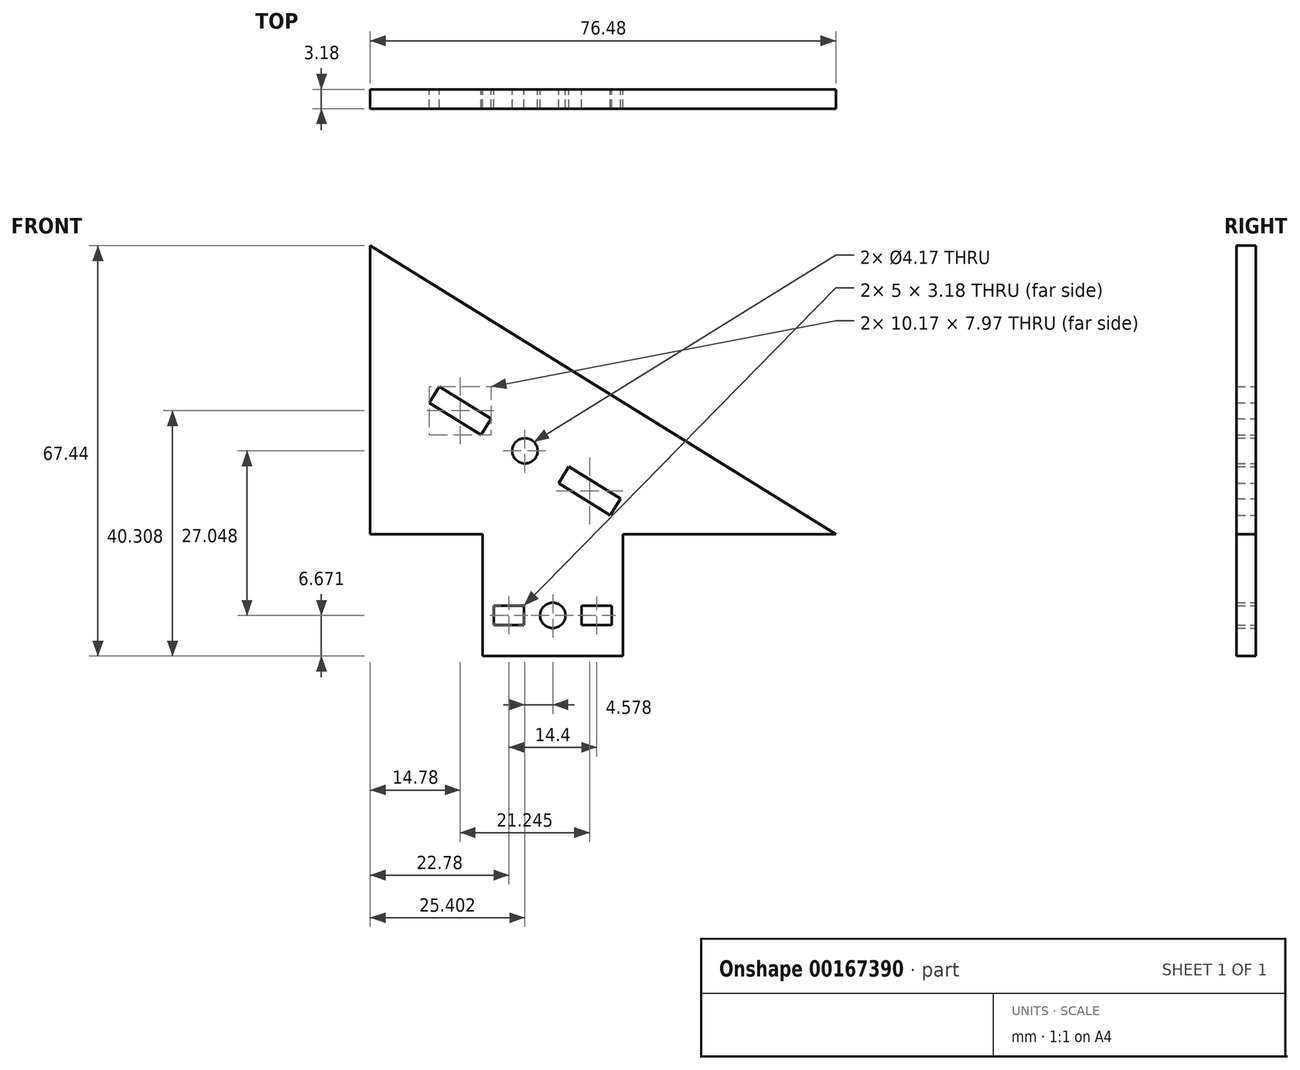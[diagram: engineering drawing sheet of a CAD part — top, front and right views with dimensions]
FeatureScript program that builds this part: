
annotation { "Feature Type Name" : "Feature", "Feature Type Description" : "" }
export const myFeature = defineFeature(function(context is Context, id is Id, definition is map)
    precondition{}
    {
        {
            var Q0;
            Q0=qCreatedBy(makeId("Front.planeOp"),FACE);
            var sketch = newSketch(context, id + "F0", { "sketchPlane" : qUnion([Q0])});
            skLineSegment(sketch, "E0", {"start": v(0, -17.4) * mm, "end": v(-11.5, -17.4) * mm});
            skLineSegment(sketch, "E1.MirrorCS", {"start": v(0, -17.4) * mm, "end": v(11.5, -17.4) * mm});
            skLineSegment(sketch, "E2", {"start": v(-11.5, -17.4) * mm, "end": v(-11.5, 2.6) * mm});
            skLineSegment(sketch, "E3", {"start": v(-9.7, -12.32) * mm, "end": v(-9.7, -9.14) * mm});
            skLineSegment(sketch, "E4", {"start": v(-9.7, -9.14) * mm, "end": v(-4.7, -9.14) * mm});
            skLineSegment(sketch, "E5", {"start": v(-9.7, -12.32) * mm, "end": v(-4.7, -12.32) * mm});
            skLineSegment(sketch, "E6", {"start": v(-4.7, -12.32) * mm, "end": v(-4.7, -9.14) * mm});
            skCircle(sketch, "E7", {"center": v(0, -10.73) * mm, "radius": 2.08 * mm});
            skLineSegment(sketch, "E8.MirrorCS", {"start": v(9.7, -12.32) * mm, "end": v(9.7, -9.14) * mm});
            skLineSegment(sketch, "E9.MirrorCS", {"start": v(9.7, -9.14) * mm, "end": v(4.7, -9.14) * mm});
            skLineSegment(sketch, "E10.MirrorCS", {"start": v(9.7, -12.32) * mm, "end": v(4.7, -12.32) * mm});
            skLineSegment(sketch, "E11.MirrorCS", {"start": v(4.7, -12.32) * mm, "end": v(4.7, -9.14) * mm});
            skLineSegment(sketch, "E12.MirrorCS", {"start": v(11.5, -17.4) * mm, "end": v(11.5, 2.6) * mm});
            skLineSegment(sketch, "E13", {"start": v(11.5, 2.6) * mm, "end": v(46.5, 2.6) * mm});
            skLineSegment(sketch, "E14", {"start": v(46.5, 2.6) * mm, "end": v(-29.98, 50.04) * mm});
            skLineSegment(sketch, "E15", {"start": v(-29.98, 50.04) * mm, "end": v(-29.98, 2.6) * mm});
            skLineSegment(sketch, "E16", {"start": v(-29.98, 2.6) * mm, "end": v(-11.5, 2.6) * mm});
            skLineSegment(sketch, "E17", {"start": v(-18.61, 26.9) * mm, "end": v(-10.11, 21.62) * mm});
            skLineSegment(sketch, "E18", {"start": v(-10.11, 21.62) * mm, "end": v(-11.79, 18.92) * mm});
            skLineSegment(sketch, "E19", {"start": v(-11.79, 18.92) * mm, "end": v(-20.29, 24.2) * mm});
            skLineSegment(sketch, "E20", {"start": v(-18.61, 26.9) * mm, "end": v(-20.29, 24.2) * mm});
            skCircle(sketch, "E21", {"center": v(-4.58, 16.32) * mm, "radius": 2.08 * mm});
            skLineSegment(sketch, "E22.MirrorCS", {"start": v(0.96, 11.02) * mm, "end": v(9.46, 5.75) * mm});
            skLineSegment(sketch, "E23.MirrorCS", {"start": v(2.63, 13.72) * mm, "end": v(0.96, 11.02) * mm});
            skLineSegment(sketch, "E24.MirrorCS", {"start": v(11.13, 8.44) * mm, "end": v(2.63, 13.72) * mm});
            skLineSegment(sketch, "E25.MirrorCS", {"start": v(11.13, 8.44) * mm, "end": v(9.46, 5.75) * mm});
            skSolve(sketch);
        }
        {
            var Q0;
            Q0 = qSketchRegion(id + "F0", true);
            extrude(context, id + "F1", {"entities" : qUnion([Q0]), "depth" : 3.17 * mm});
        }
    });
